annotation { "Feature Type Name" : "Feature", "Feature Type Description" : "" }
export const myFeature = defineFeature(function(context is Context, id is Id, definition is map)
    precondition{}
    {
        {
            var Q0;
            Q0=qCreatedBy(makeId("Front.planeOp"),FACE);
            var sketch = newSketch(context, id + "F0", { "sketchPlane" : qUnion([Q0])});
            skText(sketch, "E0", { "text": "FLAT FOUR", "fontName": "NotoSerif-Bold.ttf"});
            const initialGuessF0  = {"E0": [-0.06883, 0, 1, 0, 0.01717]};
            skSetInitialGuess(sketch, initialGuessF0);
            skSolve(sketch);
        }
        {
            var Q0;
            Q0=qCreatedBy(makeId("Front.planeOp"),FACE);
            var sketch = newSketch(context, id + "F1", { "sketchPlane" : qUnion([Q0])});
            skLineSegment(sketch, "E1.bottom", {"start": v(-64.91, 0) * mm, "end": v(-63.91, 0) * mm});
            skLineSegment(sketch, "E1.top", {"start": v(-64.91, -4) * mm, "end": v(-63.91, -4) * mm});
            skLineSegment(sketch, "E1.left", {"start": v(-64.91, 0) * mm, "end": v(-64.91, -4) * mm});
            skLineSegment(sketch, "E1.right", {"start": v(-63.91, 0) * mm, "end": v(-63.91, -4) * mm});
            skSolve(sketch);
        }
        {
            var Q0;
            Q0 = qSketchRegion(id + "F0", true);
            extrude(context, id + "F2", {"entities" : qUnion([Q0]), "oppositeDirection" : true, "depth" : 4 * mm, "offsetDistance" : 25 * mm});
        }
        {
            var Q0;
            Q0 = qSketchRegion(id + "F1", true);
            extrude(context, id + "F3", {"entities" : qUnion([Q0]), "operationType" : NewBodyOperationType.ADD, "oppositeDirection" : true, "depth" : 4 * mm, "offsetDistance" : 25 * mm});
        }
        {
            var Q0;
            Q0=makeQuery(id+"F2.opExtrude","SWEPT_FACE",FACE,{"disambiguationData":[OSD([sQuery(id+"F0.wireOp",EDGE,"E0.sketch_text.stroke-59")])]});
            var sketch = newSketch(context, id + "F4", { "sketchPlane" : qUnion([Q0])});
            skLineSegment(sketch, "E2.bottom", {"start": v(-47.37, 0) * mm, "end": v(-46.37, 0) * mm});
            skLineSegment(sketch, "E2.top", {"start": v(-47.37, -4) * mm, "end": v(-46.37, -4) * mm});
            skLineSegment(sketch, "E2.left", {"start": v(-47.37, 0) * mm, "end": v(-47.37, -4) * mm});
            skLineSegment(sketch, "E2.right", {"start": v(-46.37, 0) * mm, "end": v(-46.37, -4) * mm});
            skSolve(sketch);
        }
        {
            var Q0;
            Q0 = qSketchRegion(id + "F4", true);
            extrude(context, id + "F5", {"entities" : qUnion([Q0]), "operationType" : NewBodyOperationType.ADD, "depth" : 4 * mm, "offsetDistance" : 25 * mm});
        }
        {
            var Q0;
            Q0=makeQuery(id+"F2.opExtrude","SWEPT_FACE",FACE,{"disambiguationData":[OSD([sQuery(id+"F0.wireOp",EDGE,"E0.sketch_text.stroke-69")])]});
            var sketch = newSketch(context, id + "F6", { "sketchPlane" : qUnion([Q0])});
            skLineSegment(sketch, "E3.bottom", {"start": v(-35.24, 0) * mm, "end": v(-34.24, 0) * mm});
            skLineSegment(sketch, "E3.top", {"start": v(-35.24, -4) * mm, "end": v(-34.24, -4) * mm});
            skLineSegment(sketch, "E3.left", {"start": v(-35.24, 0) * mm, "end": v(-35.24, -4) * mm});
            skLineSegment(sketch, "E3.right", {"start": v(-34.24, 0) * mm, "end": v(-34.24, -4) * mm});
            skSolve(sketch);
        }
        {
            var Q0;
            Q0=makeQuery(id+"F6.imprint","IMPRINT",FACE,{"disambiguationData":[TD([[makeQuery(id+"F6.imprint","IMPRINT",EDGE,{"derivedFrom":sQuery(id+"F6.wireOp",EDGE,"E3.bottom")}),1.0]])]});
            extrude(context, id + "F7", {"entities" : qUnion([Q0]), "operationType" : NewBodyOperationType.ADD, "depth" : 4 * mm, "offsetDistance" : 25 * mm});
        }
        {
            var Q0;
            Q0=makeQuery(id+"F2.opExtrude","SWEPT_FACE",FACE,{"disambiguationData":[OSD([sQuery(id+"F0.wireOp",EDGE,"E0.sketch_text.stroke-85")])]});
            var sketch = newSketch(context, id + "F8", { "sketchPlane" : qUnion([Q0])});
            skLineSegment(sketch, "E4.bottom", {"start": v(-24.42, 0) * mm, "end": v(-23.42, 0) * mm});
            skLineSegment(sketch, "E4.top", {"start": v(-24.42, -4) * mm, "end": v(-23.42, -4) * mm});
            skLineSegment(sketch, "E4.left", {"start": v(-24.42, 0) * mm, "end": v(-24.42, -4) * mm});
            skLineSegment(sketch, "E4.right", {"start": v(-23.42, 0) * mm, "end": v(-23.42, -4) * mm});
            skSolve(sketch);
        }
        {
            var Q0;
            Q0=makeQuery(id+"F8.imprint","IMPRINT",FACE,{"disambiguationData":[TD([[makeQuery(id+"F8.imprint","IMPRINT",EDGE,{"derivedFrom":sQuery(id+"F8.wireOp",EDGE,"E4.bottom")}),1.0]])]});
            extrude(context, id + "F9", {"entities" : qUnion([Q0]), "operationType" : NewBodyOperationType.ADD, "depth" : 4 * mm, "offsetDistance" : 25 * mm});
        }
        {
            var Q0;
            Q0=makeQuery(id+"F2.opExtrude","SWEPT_FACE",FACE,{"disambiguationData":[OSD([sQuery(id+"F0.wireOp",EDGE,"E0.sketch_text.stroke-113")])]});
            var sketch = newSketch(context, id + "F10", { "sketchPlane" : qUnion([Q0])});
            skLineSegment(sketch, "E5.bottom", {"start": v(-12.99, 0) * mm, "end": v(-11.99, 0) * mm});
            skLineSegment(sketch, "E5.top", {"start": v(-12.99, -4) * mm, "end": v(-11.99, -4) * mm});
            skLineSegment(sketch, "E5.left", {"start": v(-12.99, 0) * mm, "end": v(-12.99, -4) * mm});
            skLineSegment(sketch, "E5.right", {"start": v(-11.99, 0) * mm, "end": v(-11.99, -4) * mm});
            skSolve(sketch);
        }
        {
            var Q0;
            Q0=makeQuery(id+"F10.imprint","IMPRINT",FACE,{"disambiguationData":[TD([[makeQuery(id+"F10.imprint","IMPRINT",EDGE,{"derivedFrom":sQuery(id+"F10.wireOp",EDGE,"E5.bottom")}),1.0]])]});
            extrude(context, id + "F11", {"entities" : qUnion([Q0]), "operationType" : NewBodyOperationType.ADD, "depth" : 4 * mm, "offsetDistance" : 25 * mm});
        }
        {
            var Q0;
            Q0=makeQuery(id+"F2.opExtrude","SWEPT_FACE",FACE,{"disambiguationData":[OSD([sQuery(id+"F0.wireOp",EDGE,"E0.sketch_text.stroke-154")])]});
            var sketch = newSketch(context, id + "F12", { "sketchPlane" : qUnion([Q0])});
            skLineSegment(sketch, "E6.bottom", {"start": v(5.76, 0) * mm, "end": v(6.76, 0) * mm});
            skLineSegment(sketch, "E6.top", {"start": v(5.76, -4) * mm, "end": v(6.76, -4) * mm});
            skLineSegment(sketch, "E6.left", {"start": v(5.76, 0) * mm, "end": v(5.76, -4) * mm});
            skLineSegment(sketch, "E6.right", {"start": v(6.76, 0) * mm, "end": v(6.76, -4) * mm});
            skSolve(sketch);
        }
        {
            var Q0;
            Q0=makeQuery(id+"F12.imprint","IMPRINT",FACE,{"disambiguationData":[TD([[makeQuery(id+"F12.imprint","IMPRINT",EDGE,{"derivedFrom":sQuery(id+"F12.wireOp",EDGE,"E6.bottom")}),1.0]])]});
            extrude(context, id + "F13", {"entities" : qUnion([Q0]), "operationType" : NewBodyOperationType.ADD, "depth" : 4 * mm, "offsetDistance" : 25 * mm});
        }
        {
            var Q0;
            Q0=qCreatedBy(makeId("Top.planeOp"),FACE);
            var sketch = newSketch(context, id + "F14", { "sketchPlane" : qUnion([Q0])});
            skLineSegment(sketch, "E7.bottom", {"start": v(24.68, 0) * mm, "end": v(25.68, 0) * mm});
            skLineSegment(sketch, "E7.top", {"start": v(24.68, 4.12) * mm, "end": v(25.68, 4.12) * mm});
            skLineSegment(sketch, "E7.left", {"start": v(24.68, 0) * mm, "end": v(24.68, 4.12) * mm});
            skLineSegment(sketch, "E7.right", {"start": v(25.68, 0) * mm, "end": v(25.68, 4.12) * mm});
            skSolve(sketch);
        }
        {
            var Q0;
            Q0 = qSketchRegion(id + "F14", true);
            extrude(context, id + "F15", {"entities" : qUnion([Q0]), "operationType" : NewBodyOperationType.ADD, "oppositeDirection" : true, "depth" : 4 * mm, "offsetDistance" : 25 * mm});
        }
        {
            var Q0;
            Q0=qCreatedBy(makeId("Top.planeOp"),FACE);
            var sketch = newSketch(context, id + "F16", { "sketchPlane" : qUnion([Q0])});
            skLineSegment(sketch, "E8.bottom", {"start": v(43.63, 0) * mm, "end": v(44.63, 0) * mm});
            skLineSegment(sketch, "E8.top", {"start": v(43.63, 4) * mm, "end": v(44.63, 4) * mm});
            skLineSegment(sketch, "E8.left", {"start": v(43.63, 0) * mm, "end": v(43.63, 4) * mm});
            skLineSegment(sketch, "E8.right", {"start": v(44.63, 0) * mm, "end": v(44.63, 4) * mm});
            skSolve(sketch);
        }
        {
            var Q0;
            Q0 = qSketchRegion(id + "F16", true);
            extrude(context, id + "F17", {"entities" : qUnion([Q0]), "operationType" : NewBodyOperationType.ADD, "oppositeDirection" : true, "depth" : 4 * mm, "offsetDistance" : 25 * mm});
        }
        {
            var Q0;
            Q0=makeQuery(id+"F2.opExtrude","SWEPT_FACE",FACE,{"disambiguationData":[OSD([sQuery(id+"F0.wireOp",EDGE,"E0.sketch_text.stroke-289")])]});
            var sketch = newSketch(context, id + "F18", { "sketchPlane" : qUnion([Q0])});
            skLineSegment(sketch, "E9.bottom", {"start": v(56.8, 0) * mm, "end": v(57.8, 0) * mm});
            skLineSegment(sketch, "E9.top", {"start": v(56.8, -4) * mm, "end": v(57.8, -4) * mm});
            skLineSegment(sketch, "E9.left", {"start": v(56.8, 0) * mm, "end": v(56.8, -4) * mm});
            skLineSegment(sketch, "E9.right", {"start": v(57.8, 0) * mm, "end": v(57.8, -4) * mm});
            skSolve(sketch);
        }
        {
            var Q0;
            Q0=makeQuery(id+"F18.imprint","IMPRINT",FACE,{"disambiguationData":[TD([[makeQuery(id+"F18.imprint","IMPRINT",EDGE,{"derivedFrom":sQuery(id+"F18.wireOp",EDGE,"E9.bottom")}),1.0]])]});
            extrude(context, id + "F19", {"entities" : qUnion([Q0]), "operationType" : NewBodyOperationType.ADD, "depth" : 4 * mm, "offsetDistance" : 25 * mm});
        }
        {
            var Q0;
            Q0=qCreatedBy(makeId("Top.planeOp"),FACE);
            cPlane(context, id + "F20", {"entities" : qUnion([Q0]), "cplaneType" : CPlaneType.OFFSET, "offset" : 4 * mm, "oppositeDirection" : true, "width" : 150 * mm, "height" : 150 * mm});
        }
        {
            var Q0;
            Q0=qCreatedBy(id+"F20.planeOp",FACE);
            var sketch = newSketch(context, id + "F21", { "sketchPlane" : qUnion([Q0])});
            skLineSegment(sketch, "E10.bottom", {"start": v(-70.15, 0) * mm, "end": v(69.85, 0) * mm});
            skLineSegment(sketch, "E10.top", {"start": v(-70.15, 4) * mm, "end": v(69.85, 4) * mm});
            skLineSegment(sketch, "E10.left", {"start": v(-70.15, 0) * mm, "end": v(-70.15, 4) * mm});
            skLineSegment(sketch, "E10.right", {"start": v(69.85, 0) * mm, "end": v(69.85, 4) * mm});
            skSolve(sketch);
        }
        {
            var Q0;
            Q0=makeQuery(id+"F21.imprint","IMPRINT",FACE,{"disambiguationData":[TD([[makeQuery(id+"F21.imprint","IMPRINT",EDGE,{"derivedFrom":sQuery(id+"F21.wireOp",EDGE,"E10.bottom")}),1.0]])]});
            extrude(context, id + "F22", {"entities" : qUnion([Q0]), "oppositeDirection" : true, "depth" : 2 * mm, "offsetDistance" : 25 * mm});
        }
        {
            var Q0;
            Q0=qCreatedBy(makeId("Top.planeOp"),FACE);
            var sketch = newSketch(context, id + "F23", { "sketchPlane" : qUnion([Q0])});
            skLineSegment(sketch, "E11.bottom", {"start": v(67.53, 0) * mm, "end": v(68.53, 0) * mm});
            skLineSegment(sketch, "E11.top", {"start": v(67.53, 4) * mm, "end": v(68.53, 4) * mm});
            skLineSegment(sketch, "E11.left", {"start": v(67.53, 0) * mm, "end": v(67.53, 4) * mm});
            skLineSegment(sketch, "E11.right", {"start": v(68.53, 0) * mm, "end": v(68.53, 4) * mm});
            skSolve(sketch);
        }
        {
            var Q0;
            Q0 = qSketchRegion(id + "F23", true);
            extrude(context, id + "F24", {"entities" : qUnion([Q0]), "operationType" : NewBodyOperationType.ADD, "oppositeDirection" : true, "depth" : 4.5 * mm, "offsetDistance" : 25 * mm});
        }
    });